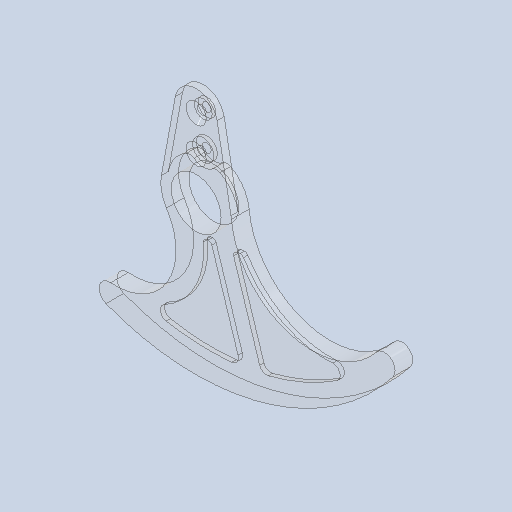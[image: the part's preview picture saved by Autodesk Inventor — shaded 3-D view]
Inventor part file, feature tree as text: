
AUTODESK INVENTOR PART (.ipt)
format: ipt  version: 2023 (Build 270158000, 158)  size: 257,536 bytes
history: native  units: mm
features: extrude x4, sketch x2, chamfer x1, projected_geometry x1
ambient origin geometry x8: Origin, YZ Plane, XZ Plane, XY Plane, X Axis, Y Axis, Z Axis, Center Point
bodies: Solid2 (feature_tree)
feature tree (8):
  sketch  "Sketch1"  dims[d0=36.0mm d1=8.05mm d2=6.0mm d3=14.0mm d4=60.0mm d5=37.0mm d6=22.0mm d7=18.0mm d8=12.0mm d9=7.05mm d10=20.0mm d11=14.05mm d12=35.0mm d13=5.0mm d14=60.0mm d15=4.073636mm d17=66.63748mm d18=64.584666mm d19=6.0mm d20=6.0mm d21=13.0mm d23=17.0mm d29=2.5mm d30=6.0mm d31=8.5mm d32=2.5mm d43=10.0mm d44=2.0mm d45=2.0mm d46=9.897985mm d47=23.0mm d48=5.0mm d49=0.0mm d50=2.0mm d51=0.0mm d52=3.0mm d53=0.0mm d54=1.6mm d55=2.0mm d56=45.0deg d57=1.0mm d58=1.0mm d59=4.0mm d60=12.857732mm d61=6.428866mm d62=3.0mm d63=1.0mm d64=4.0mm d66=2.0mm d67=4.0mm d68=2.0mm d70=3.0mm d71=1.0mm d72=1.0mm d73=4.0mm d74=4.0mm d75=2.0mm d76=2.0mm d77=4.0mm d78=1.2mm d79=0.0mm]
  extrude  "Extrusion5"  Depth=2.5mm
  extrude  "Extrusion6"  Depth=6.0mm
  extrude  "Extrusion7"  Depth=1.2mm
  chamfer  "Chamfer3"  Distance=2.5mm
  extrude  "押し出し8"  Depth=10.0mm
  sketch  "スケッチ5"
  projected_geometry  "投影ループ1"
